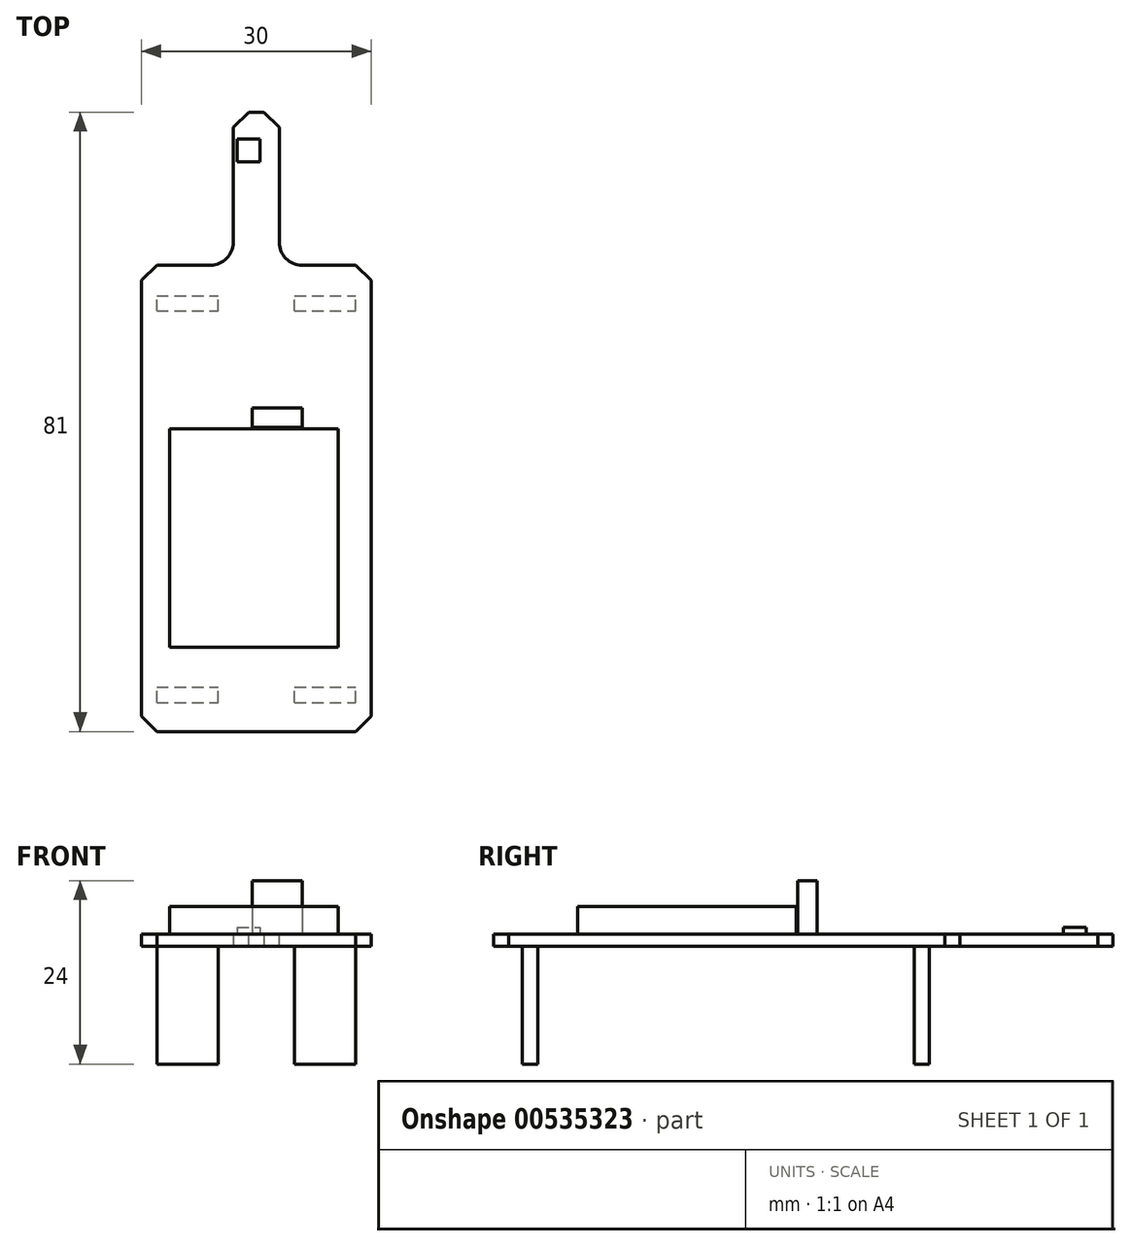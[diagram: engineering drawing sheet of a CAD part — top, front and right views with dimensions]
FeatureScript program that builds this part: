
annotation { "Feature Type Name" : "Feature", "Feature Type Description" : "" }
export const myFeature = defineFeature(function(context is Context, id is Id, definition is map)
    precondition{}
    {
        {
            var Q0;
            Q0=qCreatedBy(makeId("Top.planeOp"),FACE);
            var sketch = newSketch(context, id + "F0", { "sketchPlane" : qUnion([Q0])});
            skLineSegment(sketch, "E0.bottom", {"start": v(-15, 30.5) * mm, "end": v(-3, 30.5) * mm});
            skLineSegment(sketch, "E0.top", {"start": v(-15, -30.5) * mm, "end": v(15, -30.5) * mm});
            skLineSegment(sketch, "E0.left", {"start": v(-15, 30.5) * mm, "end": v(-15, -30.5) * mm});
            skLineSegment(sketch, "E0.right", {"start": v(15, 30.5) * mm, "end": v(15, -30.5) * mm});
            skLineSegment(sketch, "E1.bottom", {"start": v(-3, 50.5) * mm, "end": v(3, 50.5) * mm});
            skLineSegment(sketch, "E1.left", {"start": v(-3, 50.5) * mm, "end": v(-3, 30.5) * mm});
            skLineSegment(sketch, "E1.right", {"start": v(3, 50.5) * mm, "end": v(3, 30.5) * mm});
            skLineSegment(sketch, "E2.trimOffspring", {"start": v(3, 30.5) * mm, "end": v(15, 30.5) * mm});
            skLineSegment(sketch, "E3", {"start": v(-15, 30.5) * mm, "end": v(15, -30.5) * mm, "construction": true});
            skLineSegment(sketch, "E4", {"start": v(15, 30.5) * mm, "end": v(-15, -30.5) * mm, "construction": true});
            skPoint(sketch, "E5", {"position": v(0, 0) * mm});
            skSolve(sketch);
        }
        {
            var Q0;
            Q0=makeQuery(id+"F0.imprint","IMPRINT",FACE,{"disambiguationData":[TD([[makeQuery(id+"F0.imprint","IMPRINT",EDGE,{"derivedFrom":sQuery(id+"F0.wireOp",EDGE,"E0.bottom")}),-1.0]])]});
            extrude(context, id + "F1", {"entities" : qUnion([Q0]), "depth" : 1.6 * mm, "offsetDistance" : 25 * mm});
        }
        {
            var Q0;
            Q0=makeQuery(id+"F1.opExtrude","CAP_FACE",FACE,{"disambiguationData":[OSD([sQuery(id+"F0.wireOp",EDGE,"E0.bottom"),sQuery(id+"F0.wireOp",EDGE,"E0.top"),sQuery(id+"F0.wireOp",EDGE,"E0.left"),sQuery(id+"F0.wireOp",EDGE,"E0.right"),sQuery(id+"F0.wireOp",EDGE,"E1.bottom"),sQuery(id+"F0.wireOp",EDGE,"E1.left"),sQuery(id+"F0.wireOp",EDGE,"E1.right"),sQuery(id+"F0.wireOp",EDGE,"E2.trimOffspring")])],"isStart":false});
            var sketch = newSketch(context, id + "F2", { "sketchPlane" : qUnion([Q0])});
            skLineSegment(sketch, "E6.bottom", {"start": v(-11.3, 9.1) * mm, "end": v(10.7, 9.1) * mm});
            skLineSegment(sketch, "E6.top", {"start": v(-11.3, -19.5) * mm, "end": v(10.7, -19.5) * mm});
            skLineSegment(sketch, "E6.left", {"start": v(-11.3, 9.1) * mm, "end": v(-11.3, -19.5) * mm});
            skLineSegment(sketch, "E6.right", {"start": v(10.7, 9.1) * mm, "end": v(10.7, -19.5) * mm});
            skLineSegment(sketch, "E7.bottom", {"start": v(-0.5, 11.8) * mm, "end": v(6, 11.8) * mm});
            skLineSegment(sketch, "E7.top", {"start": v(-0.5, 9.3) * mm, "end": v(6, 9.3) * mm});
            skLineSegment(sketch, "E7.left", {"start": v(-0.5, 11.8) * mm, "end": v(-0.5, 9.3) * mm});
            skLineSegment(sketch, "E7.right", {"start": v(6, 11.8) * mm, "end": v(6, 9.3) * mm});
            skLineSegment(sketch, "E8.bottom", {"start": v(-2.5, 47) * mm, "end": v(0.5, 47) * mm});
            skLineSegment(sketch, "E8.top", {"start": v(-2.5, 44) * mm, "end": v(0.5, 44) * mm});
            skLineSegment(sketch, "E8.left", {"start": v(-2.5, 47) * mm, "end": v(-2.5, 44) * mm});
            skLineSegment(sketch, "E8.right", {"start": v(0.5, 47) * mm, "end": v(0.5, 44) * mm});
            skSolve(sketch);
        }
        {
            var Q0;
            Q0=makeQuery(id+"F2.imprint","IMPRINT",FACE,{"disambiguationData":[TD([[makeQuery(id+"F2.imprint","IMPRINT",EDGE,{"derivedFrom":sQuery(id+"F2.wireOp",EDGE,"E6.bottom")}),-1.0]])]});
            extrude(context, id + "F3", {"entities" : qUnion([Q0]), "operationType" : NewBodyOperationType.ADD, "depth" : 3.6 * mm, "offsetDistance" : 25 * mm});
        }
        {
            var Q0;
            Q0=makeQuery(id+"F2.imprint","IMPRINT",FACE,{"disambiguationData":[TD([[makeQuery(id+"F2.imprint","IMPRINT",EDGE,{"derivedFrom":sQuery(id+"F2.wireOp",EDGE,"E7.bottom")}),-1.0]])]});
            extrude(context, id + "F4", {"entities" : qUnion([Q0]), "operationType" : NewBodyOperationType.ADD, "depth" : 7 * mm, "offsetDistance" : 25 * mm});
        }
        {
            var Q0;
            Q0=makeQuery(id+"F2.imprint","IMPRINT",FACE,{"disambiguationData":[TD([[makeQuery(id+"F2.imprint","IMPRINT",EDGE,{"derivedFrom":sQuery(id+"F2.wireOp",EDGE,"E8.bottom")}),-1.0]])]});
            extrude(context, id + "F5", {"entities" : qUnion([Q0]), "operationType" : NewBodyOperationType.ADD, "depth" : .9 * mm, "offsetDistance" : 25 * mm});
        }
        {
            var Q0;
            Q0=makeQuery(id+"F1.opExtrude","CAP_FACE",FACE,{"disambiguationData":[OSD([sQuery(id+"F0.wireOp",EDGE,"E0.bottom"),sQuery(id+"F0.wireOp",EDGE,"E0.top"),sQuery(id+"F0.wireOp",EDGE,"E0.left"),sQuery(id+"F0.wireOp",EDGE,"E0.right"),sQuery(id+"F0.wireOp",EDGE,"E1.bottom"),sQuery(id+"F0.wireOp",EDGE,"E1.left"),sQuery(id+"F0.wireOp",EDGE,"E1.right"),sQuery(id+"F0.wireOp",EDGE,"E2.trimOffspring")])],"isStart":true});
            var sketch = newSketch(context, id + "F6", { "sketchPlane" : qUnion([Q0])});
            skLineSegment(sketch, "E9.bottom", {"start": v(-13, 26.7) * mm, "end": v(-5, 26.7) * mm});
            skLineSegment(sketch, "E9.top", {"start": v(-13, 24.7) * mm, "end": v(-5, 24.7) * mm});
            skLineSegment(sketch, "E9.left", {"start": v(-13, 26.7) * mm, "end": v(-13, 24.7) * mm});
            skLineSegment(sketch, "E9.right", {"start": v(-5, 26.7) * mm, "end": v(-5, 24.7) * mm});
            skLineSegment(sketch, "E10.bottom", {"start": v(5, 26.7) * mm, "end": v(13, 26.7) * mm});
            skLineSegment(sketch, "E10.top", {"start": v(5, 24.7) * mm, "end": v(13, 24.7) * mm});
            skLineSegment(sketch, "E10.left", {"start": v(5, 26.7) * mm, "end": v(5, 24.7) * mm});
            skLineSegment(sketch, "E10.right", {"start": v(13, 26.7) * mm, "end": v(13, 24.7) * mm});
            skLineSegment(sketch, "E11.bottom", {"start": v(-13, -24.5) * mm, "end": v(-5, -24.5) * mm});
            skLineSegment(sketch, "E11.top", {"start": v(-13, -26.5) * mm, "end": v(-5, -26.5) * mm});
            skLineSegment(sketch, "E11.left", {"start": v(-13, -24.5) * mm, "end": v(-13, -26.5) * mm});
            skLineSegment(sketch, "E11.right", {"start": v(-5, -24.5) * mm, "end": v(-5, -26.5) * mm});
            skLineSegment(sketch, "E12.bottom", {"start": v(5, -24.5) * mm, "end": v(13, -24.5) * mm});
            skLineSegment(sketch, "E12.top", {"start": v(5, -26.5) * mm, "end": v(13, -26.5) * mm});
            skLineSegment(sketch, "E12.left", {"start": v(5, -24.5) * mm, "end": v(5, -26.5) * mm});
            skLineSegment(sketch, "E12.right", {"start": v(13, -24.5) * mm, "end": v(13, -26.5) * mm});
            skLineSegment(sketch, "E13.0", {"start": v(3, -30.5) * mm, "end": v(15, -30.5) * mm});
            skPoint(sketch, "E13.1", {"position": v(9, -30.5) * mm});
            skLineSegment(sketch, "E14.bottom", {"start": v(5, 24.7) * mm, "end": v(-5, 24.7) * mm, "construction": true});
            skLineSegment(sketch, "E14.top", {"start": v(5, -24.7) * mm, "end": v(-5, -24.7) * mm, "construction": true});
            skLineSegment(sketch, "E14.left", {"start": v(5, 24.7) * mm, "end": v(5, -24.7) * mm, "construction": true});
            skLineSegment(sketch, "E14.right", {"start": v(-5, 24.7) * mm, "end": v(-5, -24.7) * mm, "construction": true});
            skPoint(sketch, "E14.middle", {"position": v(0, 0) * mm});
            skSolve(sketch);
        }
        {
            var Q0;
            Q0=makeQuery(id+"F6.imprint","IMPRINT",FACE,{"disambiguationData":[TD([[makeQuery(id+"F6.imprint","IMPRINT",EDGE,{"derivedFrom":sQuery(id+"F6.wireOp",EDGE,"E9.bottom")}),-1.0]])]});
            var Q1;
            Q1=makeQuery(id+"F6.imprint","IMPRINT",FACE,{"disambiguationData":[TD([[makeQuery(id+"F6.imprint","IMPRINT",EDGE,{"derivedFrom":sQuery(id+"F6.wireOp",EDGE,"E10.bottom")}),-1.0]])]});
            var Q2;
            Q2=makeQuery(id+"F6.imprint","IMPRINT",FACE,{"disambiguationData":[TD([[makeQuery(id+"F6.imprint","IMPRINT",EDGE,{"derivedFrom":sQuery(id+"F6.wireOp",EDGE,"E11.bottom")}),-1.0]])]});
            var Q3;
            Q3=makeQuery(id+"F6.imprint","IMPRINT",FACE,{"disambiguationData":[TD([[makeQuery(id+"F6.imprint","IMPRINT",EDGE,{"derivedFrom":sQuery(id+"F6.wireOp",EDGE,"E12.bottom")}),-1.0]])]});
            extrude(context, id + "F7", {"entities" : qUnion([Q0, Q1, Q2, Q3]), "operationType" : NewBodyOperationType.ADD, "depth" : 15.4 * mm, "offsetDistance" : 25 * mm});
        }
        {
            var Q0;
            Q0=makeQuery(id+"F1.opExtrude","SWEPT_EDGE",EDGE,{"disambiguationData":[OSD([sQuery(id+"F0.wireOp",EDGE,"E0.bottom"),sQuery(id+"F0.wireOp",EDGE,"E1.left")])]});
            var Q1;
            Q1=makeQuery(id+"F1.opExtrude","SWEPT_EDGE",EDGE,{"disambiguationData":[OSD([sQuery(id+"F0.wireOp",EDGE,"E1.right"),sQuery(id+"F0.wireOp",EDGE,"E2.trimOffspring")])]});
            fillet(context, id + "F8", {"entities" : qUnion([Q0, Q1]), "radius" : 3 * mm, "tangentPropagation" : true, "allowEdgeOverflow" : false});
        }
        {
            var Q0;
            Q0=makeQuery(id+"F1.opExtrude","SWEPT_EDGE",EDGE,{"disambiguationData":[OSD([sQuery(id+"F0.wireOp",EDGE,"E0.bottom"),sQuery(id+"F0.wireOp",EDGE,"E0.left")])]});
            var Q1;
            Q1=makeQuery(id+"F1.opExtrude","SWEPT_EDGE",EDGE,{"disambiguationData":[OSD([sQuery(id+"F0.wireOp",EDGE,"E0.top"),sQuery(id+"F0.wireOp",EDGE,"E0.left")])]});
            var Q2;
            Q2=makeQuery(id+"F1.opExtrude","SWEPT_EDGE",EDGE,{"disambiguationData":[OSD([sQuery(id+"F0.wireOp",EDGE,"E0.top"),sQuery(id+"F0.wireOp",EDGE,"E0.right")])]});
            var Q3;
            Q3=makeQuery(id+"F1.opExtrude","SWEPT_EDGE",EDGE,{"disambiguationData":[OSD([sQuery(id+"F0.wireOp",EDGE,"E0.right"),sQuery(id+"F0.wireOp",EDGE,"E2.trimOffspring")])]});
            var Q4;
            Q4=makeQuery(id+"F1.opExtrude","SWEPT_EDGE",EDGE,{"disambiguationData":[OSD([sQuery(id+"F0.wireOp",EDGE,"E1.bottom"),sQuery(id+"F0.wireOp",EDGE,"E1.right")])]});
            var Q5;
            Q5=makeQuery(id+"F1.opExtrude","SWEPT_EDGE",EDGE,{"disambiguationData":[OSD([sQuery(id+"F0.wireOp",EDGE,"E1.bottom"),sQuery(id+"F0.wireOp",EDGE,"E1.left")])]});
            chamfer(context, id + "F9", {"entities" : qUnion([Q0, Q1, Q2, Q3, Q4, Q5]), "width" : 2 * mm, "tangentPropagation" : true});
        }
    });
